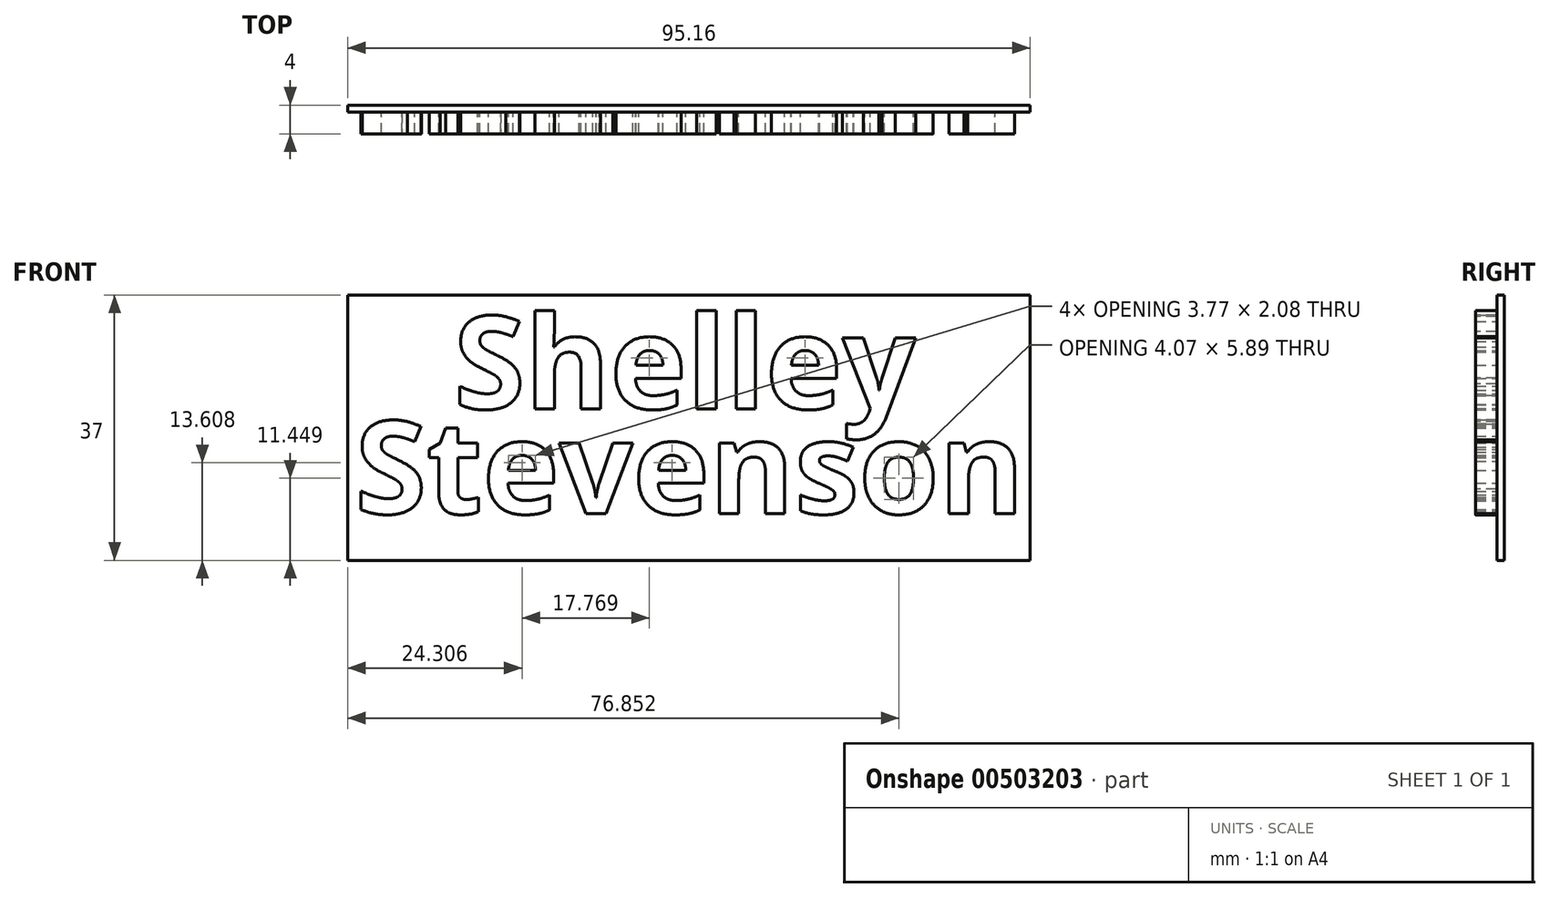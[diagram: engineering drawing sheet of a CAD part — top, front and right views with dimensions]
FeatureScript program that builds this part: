
annotation { "Feature Type Name" : "Feature", "Feature Type Description" : "" }
export const myFeature = defineFeature(function(context is Context, id is Id, definition is map)
    precondition{}
    {
        {
            var Q0;
            Q0=qCreatedBy(makeId("Front.planeOp"),FACE);
            var sketch = newSketch(context, id + "F0", { "sketchPlane" : qUnion([Q0])});
            skText(sketch, "E0", { "text": "Shelley\n", "fontName": "OpenSans-Bold.ttf"});
            const initialGuessF0  = {"E0": [-0.0328, 0, 1, 0, 0.013]};
            skSetInitialGuess(sketch, initialGuessF0);
            skSolve(sketch);
        }
        {
            var Q0;
            Q0 = qSketchRegion(id + "F0", true);
            extrude(context, id + "F1", {"entities" : qUnion([Q0]), "depth" : 3 * mm});
        }
        {
            var Q0;
            Q0=qCreatedBy(makeId("Front.planeOp"),FACE);
            var sketch = newSketch(context, id + "F2", { "sketchPlane" : qUnion([Q0])});
            skText(sketch, "E1", { "text": "Stevenson", "fontName": "OpenSans-Bold.ttf"});
            const initialGuessF2  = {"E1": [-0.04654, -0.01463, 1, 0, 0.013]};
            skSetInitialGuess(sketch, initialGuessF2);
            skSolve(sketch);
        }
        {
            var Q0;
            Q0 = qSketchRegion(id + "F2", true);
            var Q1;
            Q1=makeQuery(id+"F1.opExtrude","CAP_FACE",FACE,{"disambiguationData":[OSD([sQuery(id+"F0.wireOp",EDGE,"E0.sketch_text.stroke-0"),sQuery(id+"F0.wireOp",EDGE,"E0.sketch_text.stroke-1"),sQuery(id+"F0.wireOp",EDGE,"E0.sketch_text.stroke-2"),sQuery(id+"F0.wireOp",EDGE,"E0.sketch_text.stroke-3"),sQuery(id+"F0.wireOp",EDGE,"E0.sketch_text.stroke-4"),sQuery(id+"F0.wireOp",EDGE,"E0.sketch_text.stroke-5"),sQuery(id+"F0.wireOp",EDGE,"E0.sketch_text.stroke-6"),sQuery(id+"F0.wireOp",EDGE,"E0.sketch_text.stroke-7"),sQuery(id+"F0.wireOp",EDGE,"E0.sketch_text.stroke-8"),sQuery(id+"F0.wireOp",EDGE,"E0.sketch_text.stroke-9"),sQuery(id+"F0.wireOp",EDGE,"E0.sketch_text.stroke-10"),sQuery(id+"F0.wireOp",EDGE,"E0.sketch_text.stroke-11"),sQuery(id+"F0.wireOp",EDGE,"E0.sketch_text.stroke-12"),sQuery(id+"F0.wireOp",EDGE,"E0.sketch_text.stroke-13"),sQuery(id+"F0.wireOp",EDGE,"E0.sketch_text.stroke-14"),sQuery(id+"F0.wireOp",EDGE,"E0.sketch_text.stroke-15"),sQuery(id+"F0.wireOp",EDGE,"E0.sketch_text.stroke-16"),sQuery(id+"F0.wireOp",EDGE,"E0.sketch_text.stroke-17"),sQuery(id+"F0.wireOp",EDGE,"E0.sketch_text.stroke-18"),sQuery(id+"F0.wireOp",EDGE,"E0.sketch_text.stroke-19"),sQuery(id+"F0.wireOp",EDGE,"E0.sketch_text.stroke-20"),sQuery(id+"F0.wireOp",EDGE,"E0.sketch_text.stroke-21"),sQuery(id+"F0.wireOp",EDGE,"E0.sketch_text.stroke-22"),sQuery(id+"F0.wireOp",EDGE,"E0.sketch_text.stroke-23"),sQuery(id+"F0.wireOp",EDGE,"E0.sketch_text.stroke-24"),sQuery(id+"F0.wireOp",EDGE,"E0.sketch_text.stroke-25"),sQuery(id+"F0.wireOp",EDGE,"E0.sketch_text.stroke-26"),sQuery(id+"F0.wireOp",EDGE,"E0.sketch_text.stroke-27")])],"isStart":false});
            extrude(context, id + "F3", {"entities" : qUnion([Q0]), "endBound" : BoundingType.UP_TO_SURFACE, "endBoundEntityFace" : qUnion([Q1]), "depth" : 25 * mm});
        }
        {
            var Q0;
            Q0=qCreatedBy(makeId("Front.planeOp"),FACE);
            var sketch = newSketch(context, id + "F4", { "sketchPlane" : qUnion([Q0])});
            skLineSegment(sketch, "E2.bottom", {"start": v(-47.58, 15.85) * mm, "end": v(47.58, 15.85) * mm});
            skLineSegment(sketch, "E2.top", {"start": v(-47.58, -21.15) * mm, "end": v(47.58, -21.15) * mm});
            skLineSegment(sketch, "E2.left", {"start": v(-47.58, 15.85) * mm, "end": v(-47.58, -21.15) * mm});
            skLineSegment(sketch, "E2.right", {"start": v(47.58, 15.85) * mm, "end": v(47.58, -21.15) * mm});
            skPoint(sketch, "E3.oppositeSnap0", {"position": v(0, -21.15) * mm});
            skLineSegment(sketch, "E3.bottom", {"start": v(0, -21.15) * mm, "end": v(0, -21.15) * mm});
            skLineSegment(sketch, "E3.top", {"start": v(0, -16.91) * mm, "end": v(0, -16.91) * mm});
            skLineSegment(sketch, "E3.left", {"start": v(0, -21.15) * mm, "end": v(0, -16.91) * mm, "construction": true});
            skLineSegment(sketch, "E3.right", {"start": v(0, -21.15) * mm, "end": v(0, -16.91) * mm, "construction": true});
            skSolve(sketch);
        }
        {
            var Q0;
            Q0 = qSketchRegion(id + "F4", true);
            extrude(context, id + "F5", {"entities" : qUnion([Q0]), "oppositeDirection" : true, "depth" : 1 * mm});
        }
    });
